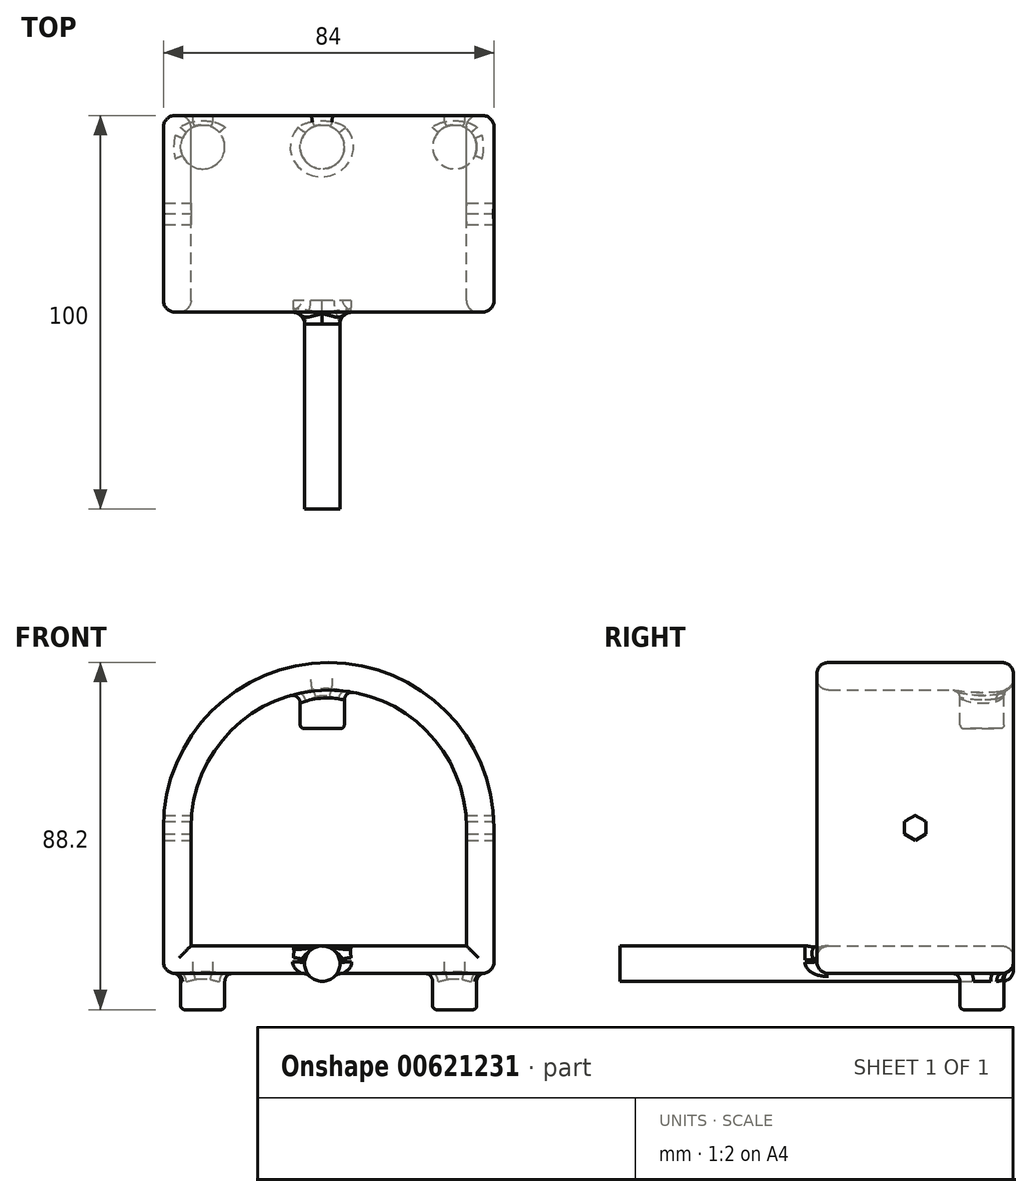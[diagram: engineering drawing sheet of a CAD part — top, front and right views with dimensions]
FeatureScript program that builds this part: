
annotation { "Feature Type Name" : "Feature", "Feature Type Description" : "" }
export const myFeature = defineFeature(function(context is Context, id is Id, definition is map)
    precondition{}
    {
        {
            var Q0;
            Q0=qCreatedBy(makeId("Front.planeOp"),FACE);
            var sketch = newSketch(context, id + "F0", { "sketchPlane" : qUnion([Q0])});
            skLineSegment(sketch, "E0", {"start": v(-23.36, 30) * mm, "end": v(26.64, 30) * mm, "construction": true});
            skCircle(sketch, "E1", {"center": v(1.64, 30) * mm, "radius": 25 * mm, "construction": true});
            skLineSegment(sketch, "E2", {"start": v(-33.36, 30) * mm, "end": v(-33.36, 0) * mm});
            skLineSegment(sketch, "E3", {"start": v(-33.36, 0) * mm, "end": v(36.64, 0) * mm});
            skLineSegment(sketch, "E4", {"start": v(36.64, 0) * mm, "end": v(36.64, 30) * mm});
            skArc(sketch, "E5", {"start": v(36.64, 30) * mm, "mid": v(1.64, 65) * mm, "end": v(-33.36, 30) * mm});
            skLineSegment(sketch, "E6.0", {"start": v(-40.36, 30) * mm, "end": v(-40.36, -7) * mm});
            skArc(sketch, "E6.1", {"start": v(43.64, 30) * mm, "mid": v(1.64, 72) * mm, "end": v(-40.36, 30) * mm});
            skLineSegment(sketch, "E6.2", {"start": v(43.64, -7) * mm, "end": v(43.64, 30) * mm});
            skLineSegment(sketch, "E6.3", {"start": v(-40.36, -7) * mm, "end": v(43.64, -7) * mm});
            skCircle(sketch, "E7", {"center": v(0, -4.5) * mm, "radius": 4.5 * mm});
            skSolve(sketch);
        }
        {
            var Q0;
            {var subQ6=sQuery(id+"F0.wireOp",EDGE,"E2");Q0=makeQuery(id+"F0.imprint","IMPRINT",FACE,{"disambiguationData":[TD([[makeQuery(id+"F0.imprint","IMPRINT",EDGE,{"derivedFrom":subQ6}),-1.0]])]});}
            var Q1;
            {var subQ0=sQuery(id+"F0.wireOp",EDGE,"E7");var subQ1=sQuery(id+"F0.wireOp",EDGE,"E6.3");var subQ2=makeQuery(id+"F0.imprint","INTERSECT",VERTEX,{"disambiguationData":[OD(0.0)],"derivedFrom":[subQ1,subQ0]});Q1=makeQuery(id+"F0.imprint","IMPRINT",FACE,{"disambiguationData":[TD([[makeQuery(id+"F0.imprint","IMPRINT",EDGE,{"disambiguationData":[TD([[subQ2,-1.0]])],"derivedFrom":subQ1}),1.0]])]});}
            extrude(context, id + "F1", {"entities" : qUnion([Q0, Q1]), "depth" : 50 * mm, "offsetDistance" : 25 * mm});
        }
        {
            var Q0;
            {var subQ0=sQuery(id+"F0.wireOp",EDGE,"E7");var subQ1=sQuery(id+"F0.wireOp",EDGE,"E6.3");var subQ2=makeQuery(id+"F0.imprint","INTERSECT",VERTEX,{"disambiguationData":[OD(0.0)],"derivedFrom":[subQ1,subQ0]});Q0=makeQuery(id+"F0.imprint","IMPRINT",FACE,{"disambiguationData":[TD([[makeQuery(id+"F0.imprint","IMPRINT",EDGE,{"disambiguationData":[TD([[subQ2,-1.0]])],"derivedFrom":subQ1}),1.0]])]});}
            var Q1;
            {var subQ0=sQuery(id+"F0.wireOp",EDGE,"E7");var subQ1=sQuery(id+"F0.wireOp",EDGE,"E6.3");var subQ2=makeQuery(id+"F0.imprint","INTERSECT",VERTEX,{"disambiguationData":[OD(0.0)],"derivedFrom":[subQ1,subQ0]});Q1=makeQuery(id+"F0.imprint","IMPRINT",FACE,{"disambiguationData":[TD([[makeQuery(id+"F0.imprint","IMPRINT",EDGE,{"disambiguationData":[TD([[subQ2,-1.0]])],"derivedFrom":subQ1}),-1.0]])]});}
            extrude(context, id + "F2", {"entities" : qUnion([Q0, Q1]), "operationType" : NewBodyOperationType.ADD, "depth" : 100 * mm, "offsetDistance" : 25 * mm});
        }
        {
            var Q0;
            Q0=makeQuery(id+"F1.opExtrude","SWEPT_FACE",FACE,{"disambiguationData":[OSD([sQuery(id+"F0.wireOp",EDGE,"E6.2")])]});
            var sketch = newSketch(context, id + "F3", { "sketchPlane" : qUnion([Q0])});
            skLineSegment(sketch, "E8", {"start": v(-50.64, 30) * mm, "end": v(0, 30) * mm, "construction": true});
            skCircle(sketch, "E9.cCircle", {"center": v(-25, 30) * mm, "radius": 2.75 * mm, "construction": true});
            skLineSegment(sketch, "E9.0", {"start": v(-22.25, 31.59) * mm, "end": v(-22.25, 28.41) * mm});
            skLineSegment(sketch, "E9.1", {"start": v(-22.25, 28.41) * mm, "end": v(-25, 26.82) * mm});
            skLineSegment(sketch, "E9.2", {"start": v(-25, 26.82) * mm, "end": v(-27.75, 28.41) * mm});
            skLineSegment(sketch, "E9.3", {"start": v(-27.75, 28.41) * mm, "end": v(-27.75, 31.59) * mm});
            skLineSegment(sketch, "E9.4", {"start": v(-27.75, 31.59) * mm, "end": v(-25, 33.18) * mm});
            skLineSegment(sketch, "E9.5", {"start": v(-25, 33.18) * mm, "end": v(-22.25, 31.59) * mm});
            skPoint(sketch, "E9.0.midPoint", {"position": v(-22.25, 30) * mm});
            skSolve(sketch);
        }
        {
            var Q0;
            {var subQ1=sQuery(id+"F3.wireOp",EDGE,"E9.4");Q0=makeQuery(id+"F3.imprint","IMPRINT",FACE,{"disambiguationData":[TD([[makeQuery(id+"F3.imprint","IMPRINT",EDGE,{"derivedFrom":subQ1}),-1.0]])]});}
            var Q1;
            {var subQ4=sQuery(id+"F3.wireOp",EDGE,"E9.1");Q1=makeQuery(id+"F3.imprint","IMPRINT",FACE,{"disambiguationData":[TD([[makeQuery(id+"F3.imprint","IMPRINT",EDGE,{"derivedFrom":subQ4}),-1.0]])]});}
            var Q2;
            Q2=makeQuery(id+"F1.opExtrude","SWEPT_FACE",FACE,{"disambiguationData":[OSD([sQuery(id+"F0.wireOp",EDGE,"E6.0")])]});
            extrude(context, id + "F4", {"entities" : qUnion([Q0, Q1]), "operationType" : NewBodyOperationType.REMOVE, "endBound" : BoundingType.UP_TO_SURFACE, "oppositeDirection" : true, "depth" : 25 * mm, "endBoundEntityFace" : qUnion([Q2]), "offsetDistance" : 25 * mm});
        }
        {
            var Q0;
            Q0=qCreatedBy(makeId("Top.planeOp"),FACE);
            cPlane(context, id + "F5", {"entities" : qUnion([Q0]), "cplaneType" : CPlaneType.OFFSET, "offset" : 65.7 * mm, "width" : 150 * mm, "height" : 150 * mm});
        }
        {
            var Q0;
            Q0=qCreatedBy(id+"F5.planeOp",FACE);
            var sketch = newSketch(context, id + "F6", { "sketchPlane" : qUnion([Q0])});
            skCircle(sketch, "E10", {"center": v(0, -8) * mm, "radius": 5.6 * mm});
            skSolve(sketch);
        }
        {
            var Q0;
            Q0=makeQuery(id+"F6.imprint","IMPRINT",FACE,{"disambiguationData":[TD([[makeQuery(id+"F6.imprint","IMPRINT",EDGE,{"derivedFrom":sQuery(id+"F6.wireOp",EDGE,"E10")}),1.0]])]});
            extrude(context, id + "F7", {"entities" : qUnion([Q0]), "operationType" : NewBodyOperationType.ADD, "oppositeDirection" : true, "depth" : 10.5 * mm, "offsetDistance" : 25 * mm});
        }
        {
            var Q0;
            Q0=qCreatedBy(makeId("Top.planeOp"),FACE);
            var sketch = newSketch(context, id + "F8", { "sketchPlane" : qUnion([Q0])});
            skCircle(sketch, "E11", {"center": v(-30.36, -8) * mm, "radius": 5.6 * mm});
            skCircle(sketch, "E12", {"center": v(33.64, -8) * mm, "radius": 5.6 * mm});
            skSolve(sketch);
        }
        {
            var Q0;
            Q0=makeQuery(id+"F8.imprint","IMPRINT",FACE,{"disambiguationData":[TD([[makeQuery(id+"F8.imprint","IMPRINT",EDGE,{"derivedFrom":sQuery(id+"F8.wireOp",EDGE,"E11")}),1.0]])]});
            var Q1;
            Q1=makeQuery(id+"F8.imprint","IMPRINT",FACE,{"disambiguationData":[TD([[makeQuery(id+"F8.imprint","IMPRINT",EDGE,{"derivedFrom":sQuery(id+"F8.wireOp",EDGE,"E12")}),1.0]])]});
            extrude(context, id + "F9", {"entities" : qUnion([Q0, Q1]), "operationType" : NewBodyOperationType.ADD, "oppositeDirection" : true, "depth" : 16.2 * mm, "offsetDistance" : 25 * mm});
        }
        {
            var Q0;
            Q0=makeQuery(id+"F7.opExtrude","CAP_EDGE",EDGE,{"disambiguationData":[OSD([sQuery(id+"F6.wireOp",EDGE,"E10")])],"isStart":false});
            var Q1;
            Q1=makeQuery(id+"F9.opExtrude","CAP_EDGE",EDGE,{"disambiguationData":[OSD([sQuery(id+"F8.wireOp",EDGE,"E11")])],"isStart":false});
            var Q2;
            Q2=makeQuery(id+"F9.opExtrude","CAP_EDGE",EDGE,{"disambiguationData":[OSD([sQuery(id+"F8.wireOp",EDGE,"E12")])],"isStart":false});
            fillet(context, id + "F10", {"entities" : qUnion([Q0, Q1, Q2]), "radius" : 1 * mm, "tangentPropagation" : true, "allowEdgeOverflow" : false});
        }
        {
            var Q0;
            Q0=makeQuery(id+"F2.boolean.opBoolean","INTERSECT",EDGE,{"disambiguationData":[OD(0.0)],"derivedFrom":[makeQuery(id+"F1.opExtrude","SWEPT_FACE",FACE,{"disambiguationData":[OSD([sQuery(id+"F0.wireOp",EDGE,"E6.3")])]}),makeQuery(id+"F2.opExtrude","SWEPT_FACE",FACE,{"disambiguationData":[OSD([sQuery(id+"F0.wireOp",EDGE,"E7")])]})]});
            var Q1;
            Q1=makeQuery(id+"F2.boolean.opBoolean","INTERSECT",EDGE,{"disambiguationData":[OD(1.0)],"derivedFrom":[makeQuery(id+"F1.opExtrude","SWEPT_FACE",FACE,{"disambiguationData":[OSD([sQuery(id+"F0.wireOp",EDGE,"E6.3")])]}),makeQuery(id+"F2.opExtrude","SWEPT_FACE",FACE,{"disambiguationData":[OSD([sQuery(id+"F0.wireOp",EDGE,"E7")])]})]});
            var Q2;
            Q2=makeQuery(id+"F2.boolean.opBoolean","INTERSECT",EDGE,{"disambiguationData":[OD(1.0)],"derivedFrom":[makeQuery(id+"F1.opExtrude","CAP_FACE",FACE,{"disambiguationData":[OSD([sQuery(id+"F0.wireOp",EDGE,"E2"),sQuery(id+"F0.wireOp",EDGE,"E3"),sQuery(id+"F0.wireOp",EDGE,"E4"),sQuery(id+"F0.wireOp",EDGE,"E5"),sQuery(id+"F0.wireOp",EDGE,"E6.0"),sQuery(id+"F0.wireOp",EDGE,"E6.1"),sQuery(id+"F0.wireOp",EDGE,"E6.2"),sQuery(id+"F0.wireOp",EDGE,"E6.3")])],"isStart":false}),makeQuery(id+"F2.opExtrude","SWEPT_FACE",FACE,{"disambiguationData":[OSD([sQuery(id+"F0.wireOp",EDGE,"E7")])]})]});
            var Q3;
            Q3=makeQuery(id+"F2.boolean.opBoolean","INTERSECT",EDGE,{"disambiguationData":[OD(0.0)],"derivedFrom":[makeQuery(id+"F1.opExtrude","CAP_FACE",FACE,{"disambiguationData":[OSD([sQuery(id+"F0.wireOp",EDGE,"E2"),sQuery(id+"F0.wireOp",EDGE,"E3"),sQuery(id+"F0.wireOp",EDGE,"E4"),sQuery(id+"F0.wireOp",EDGE,"E5"),sQuery(id+"F0.wireOp",EDGE,"E6.0"),sQuery(id+"F0.wireOp",EDGE,"E6.1"),sQuery(id+"F0.wireOp",EDGE,"E6.2"),sQuery(id+"F0.wireOp",EDGE,"E6.3")])],"isStart":false}),makeQuery(id+"F2.opExtrude","SWEPT_FACE",FACE,{"disambiguationData":[OSD([sQuery(id+"F0.wireOp",EDGE,"E7")])]})]});
            var Q4;
            {var subQ0=sQuery(id+"F0.wireOp",EDGE,"E2");var subQ1=sQuery(id+"F0.wireOp",EDGE,"E3");Q4=makeQuery(id+"F2.boolean.opBoolean","SPLIT",EDGE,{"disambiguationData":[TD([makeQuery(id+"F1.opExtrude","SWEPT_FACE",FACE,{"disambiguationData":[OSD([subQ0])]})])],"derivedFrom":makeQuery(id+"F1.opExtrude","CAP_EDGE",EDGE,{"disambiguationData":[OSD([subQ1])],"isStart":false})});}
            var Q5;
            {var subQ0=sQuery(id+"F0.wireOp",EDGE,"E4");var subQ1=sQuery(id+"F0.wireOp",EDGE,"E3");Q5=makeQuery(id+"F2.boolean.opBoolean","SPLIT",EDGE,{"disambiguationData":[TD([makeQuery(id+"F1.opExtrude","SWEPT_FACE",FACE,{"disambiguationData":[OSD([subQ0])]})])],"derivedFrom":makeQuery(id+"F1.opExtrude","CAP_EDGE",EDGE,{"disambiguationData":[OSD([subQ1])],"isStart":false})});}
            var Q6;
            Q6=makeQuery(id+"F1.opExtrude","CAP_EDGE",EDGE,{"disambiguationData":[OSD([sQuery(id+"F0.wireOp",EDGE,"E4")])],"isStart":false});
            var Q7;
            Q7=makeQuery(id+"F1.opExtrude","CAP_EDGE",EDGE,{"disambiguationData":[OSD([sQuery(id+"F0.wireOp",EDGE,"E6.2")])],"isStart":false});
            var Q8;
            Q8=makeQuery(id+"F1.opExtrude","CAP_FACE",FACE,{"disambiguationData":[OSD([sQuery(id+"F0.wireOp",EDGE,"E2"),sQuery(id+"F0.wireOp",EDGE,"E3"),sQuery(id+"F0.wireOp",EDGE,"E4"),sQuery(id+"F0.wireOp",EDGE,"E5"),sQuery(id+"F0.wireOp",EDGE,"E6.0"),sQuery(id+"F0.wireOp",EDGE,"E6.1"),sQuery(id+"F0.wireOp",EDGE,"E6.2"),sQuery(id+"F0.wireOp",EDGE,"E6.3")])],"isStart":false});
            var Q9;
            Q9=makeQuery(id+"F2.boolean.opBoolean","MERGE",FACE,{"derivedFrom":[makeQuery(id+"F1.opExtrude","CAP_FACE",FACE,{"disambiguationData":[OSD([sQuery(id+"F0.wireOp",EDGE,"E2"),sQuery(id+"F0.wireOp",EDGE,"E3"),sQuery(id+"F0.wireOp",EDGE,"E4"),sQuery(id+"F0.wireOp",EDGE,"E5"),sQuery(id+"F0.wireOp",EDGE,"E6.0"),sQuery(id+"F0.wireOp",EDGE,"E6.1"),sQuery(id+"F0.wireOp",EDGE,"E6.2"),sQuery(id+"F0.wireOp",EDGE,"E6.3")])],"isStart":true}),makeQuery(id+"F2.opExtrude","CAP_FACE",FACE,{"disambiguationData":[OSD([sQuery(id+"F0.wireOp",EDGE,"E7")])],"isStart":true})]});
            var Q10;
            Q10=makeQuery(id+"F1.opExtrude","SWEPT_EDGE",EDGE,{"disambiguationData":[OSD([sQuery(id+"F0.wireOp",EDGE,"E6.2"),sQuery(id+"F0.wireOp",EDGE,"E6.3")])]});
            var Q11;
            Q11=makeQuery(id+"F1.opExtrude","SWEPT_EDGE",EDGE,{"disambiguationData":[OSD([sQuery(id+"F0.wireOp",EDGE,"E6.0"),sQuery(id+"F0.wireOp",EDGE,"E6.3")])]});
            fillet(context, id + "F11", {"entities" : qUnion([Q0, Q1, Q2, Q3, Q4, Q5, Q6, Q7, Q8, Q9, Q10, Q11]), "radius" : 3 * mm, "tangentPropagation" : true, "allowEdgeOverflow" : false});
        }
        {
            var Q0;
            Q0=makeQuery(id+"F7.boolean.opBoolean","INTERSECT",EDGE,{"derivedFrom":[makeQuery(id+"F1.opExtrude","SWEPT_FACE",FACE,{"disambiguationData":[OSD([sQuery(id+"F0.wireOp",EDGE,"E5")])]}),makeQuery(id+"F7.opExtrude","SWEPT_FACE",FACE,{"disambiguationData":[OSD([sQuery(id+"F6.wireOp",EDGE,"E10")])]})]});
            var Q1;
            {var subQ0=sQuery(id+"F0.wireOp",EDGE,"E6.2");var subQ1=sQuery(id+"F0.wireOp",EDGE,"E6.3");Q1=makeQuery(id+"F9.boolean.opBoolean","INTERSECT",EDGE,{"derivedFrom":[makeQuery(id+"F2.boolean.opBoolean","SPLIT",FACE,{"disambiguationData":[TD([makeQuery(id+"F1.opExtrude","SWEPT_FACE",FACE,{"disambiguationData":[OSD([subQ0])]})])],"derivedFrom":makeQuery(id+"F1.opExtrude","SWEPT_FACE",FACE,{"disambiguationData":[OSD([subQ1])]})}),makeQuery(id+"F9.opExtrude","SWEPT_FACE",FACE,{"disambiguationData":[OSD([sQuery(id+"F8.wireOp",EDGE,"E12")])]})]});}
            var Q2;
            {var subQ0=sQuery(id+"F0.wireOp",EDGE,"E6.3");var subQ3=sQuery(id+"F0.wireOp",EDGE,"E6.0");Q2=makeQuery(id+"F9.boolean.opBoolean","INTERSECT",EDGE,{"derivedFrom":[makeQuery(id+"F2.boolean.opBoolean","SPLIT",FACE,{"disambiguationData":[TD([makeQuery(id+"F1.opExtrude","SWEPT_FACE",FACE,{"disambiguationData":[OSD([subQ3])]})])],"derivedFrom":makeQuery(id+"F1.opExtrude","SWEPT_FACE",FACE,{"disambiguationData":[OSD([subQ0])]})}),makeQuery(id+"F9.opExtrude","SWEPT_FACE",FACE,{"disambiguationData":[OSD([sQuery(id+"F8.wireOp",EDGE,"E11")])]})]});}
            fillet(context, id + "F12", {"entities" : qUnion([Q0, Q1, Q2]), "radius" : 2 * mm, "tangentPropagation" : true, "allowEdgeOverflow" : false});
        }
    });
